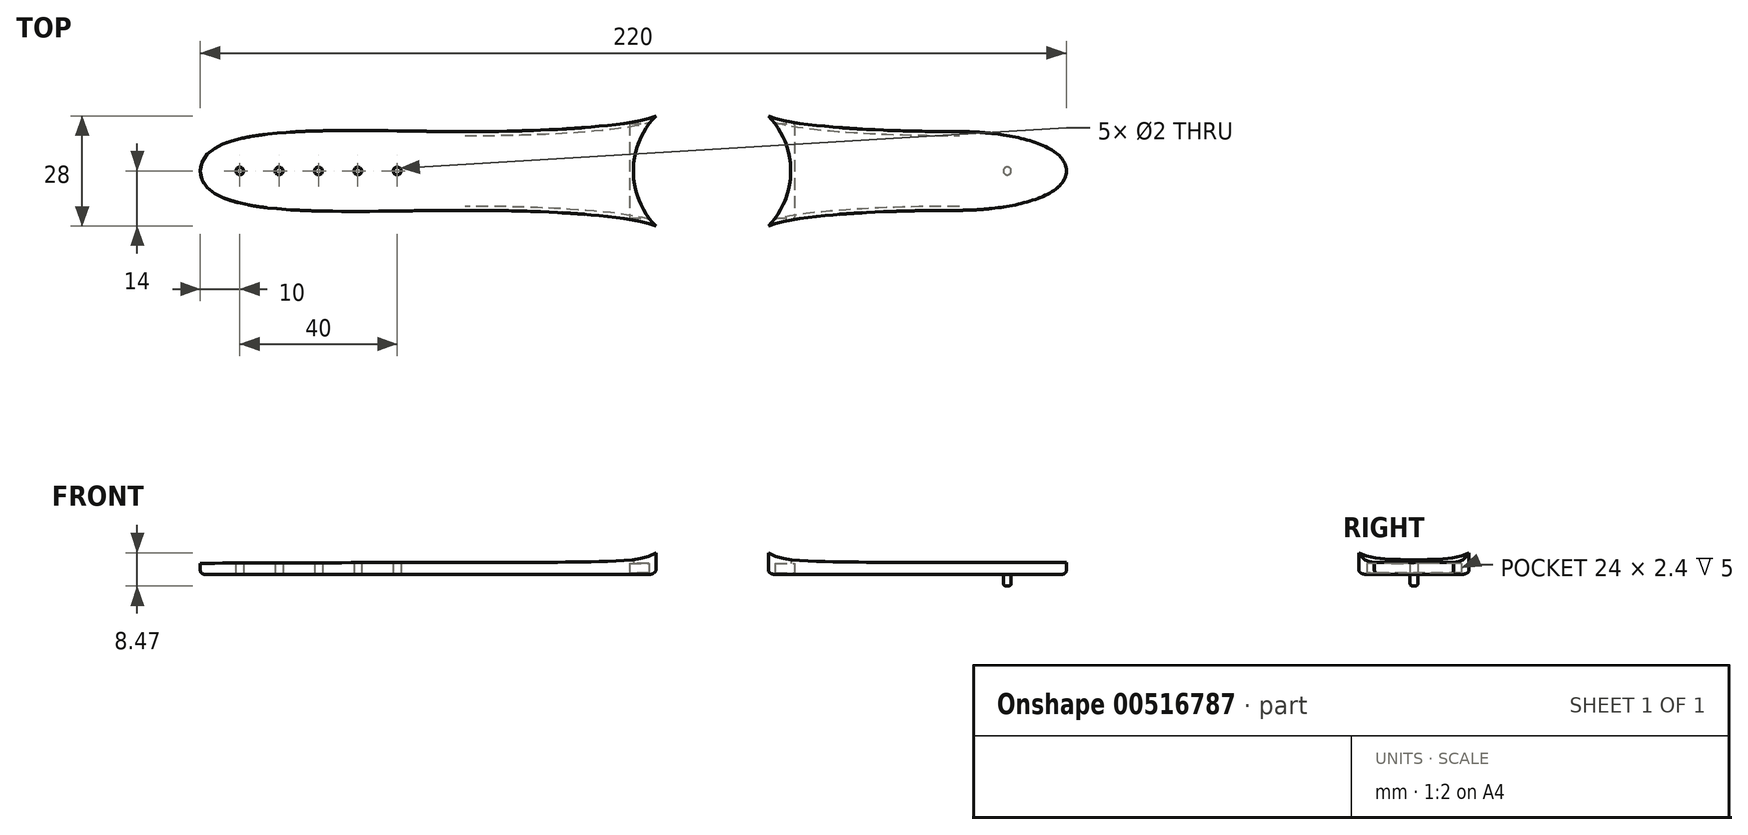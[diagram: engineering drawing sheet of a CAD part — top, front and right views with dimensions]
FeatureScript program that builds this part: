
annotation { "Feature Type Name" : "Feature", "Feature Type Description" : "" }
export const myFeature = defineFeature(function(context is Context, id is Id, definition is map)
    precondition{}
    {
        {
            var Q0;
            Q0=qCreatedBy(makeId("Top.planeOp"),FACE);
            var sketch = newSketch(context, id + "F0", { "sketchPlane" : qUnion([Q0])});
            skArc(sketch, "E0", {"start": v(-14.28, 14) * mm, "mid": v(-20, 0) * mm, "end": v(-14.28, -14) * mm});
            skFitSpline(sketch, "E1", {"points": [v(-14.28, 14) * mm, v(-62.8, 10) * mm], "startDerivative": vector(-9.22, -5.33) * mm, "endDerivative": vector(-87.74, 0) * mm});
            skLineSegment(sketch, "E2", {"start": v(-62.8, 10) * mm, "end": v(-62.8, 10) * mm});
            skFitSpline(sketch, "E3", {"points": [v(-62.8, 10) * mm, v(-130, 0) * mm], "startDerivative": vector(-91.88, 0) * mm, "endDerivative": vector(0, -38.55) * mm});
            skFitSpline(sketch, "E4.MirrorCS", {"points": [v(-14.28, -14) * mm, v(-62.8, -10) * mm], "startDerivative": vector(-9.22, 5.33) * mm, "endDerivative": vector(-87.74, 0) * mm});
            skLineSegment(sketch, "E5.MirrorCS", {"start": v(-62.8, -10) * mm, "end": v(-62.8, -10) * mm});
            skFitSpline(sketch, "E6.MirrorCS", {"points": [v(-62.8, -10) * mm, v(-130, 0) * mm], "startDerivative": vector(-91.88, 0) * mm, "endDerivative": vector(0, 38.55) * mm});
            skArc(sketch, "E7.MirrorCS", {"start": v(14.28, 14) * mm, "mid": v(20, 0) * mm, "end": v(14.28, -14) * mm});
            skFitSpline(sketch, "E8.MirrorCS", {"points": [v(14.28, 14) * mm, v(62.8, 10) * mm], "startDerivative": vector(9.22, -5.33) * mm, "endDerivative": vector(87.74, 0) * mm});
            skFitSpline(sketch, "E9.MirrorCS", {"points": [v(14.28, -14) * mm, v(62.8, -10) * mm], "startDerivative": vector(9.22, 5.33) * mm, "endDerivative": vector(87.74, 0) * mm});
            skLineSegment(sketch, "E10", {"start": v(62.8, 10) * mm, "end": v(62.8, 10) * mm});
            skLineSegment(sketch, "E11.MirrorCS", {"start": v(62.8, -10) * mm, "end": v(62.8, -10) * mm});
            skFitSpline(sketch, "E12.MirrorCS", {"points": [v(62.8, -10) * mm, v(90, 0) * mm], "startDerivative": vector(33.22, 0) * mm, "endDerivative": vector(0, 21.8) * mm});
            skFitSpline(sketch, "E13.MirrorCS", {"points": [v(62.8, 10) * mm, v(90, 0) * mm], "startDerivative": vector(33.22, 0) * mm, "endDerivative": vector(0, -21.8) * mm});
            skSolve(sketch);
        }
        {
            var Q0;
            Q0=qSketchRegion(id+"F0",true);
            extrude(context, id + "F1", {"entities" : qUnion([Q0]), "depth" : (5.5) * mm});
        }
        {
            var Q0;
            Q0=qCreatedBy(makeId("Front.planeOp"),FACE);
            var sketch = newSketch(context, id + "F2", { "sketchPlane" : qUnion([Q0])});
            skLineSegment(sketch, "E14", {"start": v(-133.54, 2.78) * mm, "end": v(-133.54, 10.44) * mm});
            skLineSegment(sketch, "E15", {"start": v(-14.23, 5.5) * mm, "end": v(-25.17, 14.96) * mm});
            skLineSegment(sketch, "E16", {"start": v(-25.17, 14.96) * mm, "end": v(-133.54, 10.44) * mm});
            skLineSegment(sketch, "E17", {"start": v(14.23, 5.5) * mm, "end": v(22.62, 12.49) * mm});
            skLineSegment(sketch, "E18", {"start": v(22.62, 12.49) * mm, "end": v(93.9, 5.99) * mm});
            skPoint(sketch, "E19", {"position": v(-133.54, 2.78) * mm});
            skFitSpline(sketch, "E20.MirrorCS", {"points": [v(14.23, 5.5) * mm, v(80, 3) * mm], "startDerivative": vector(15.03, -7.53) * mm, "endDerivative": vector(188.68, 0) * mm});
            skFitSpline(sketch, "E21.MirrorCS", {"points": [v(-14.23, 5.5) * mm, v(-80, 3) * mm], "startDerivative": vector(-15.03, -7.53) * mm, "endDerivative": vector(-188.68, 0) * mm});
            skLineSegment(sketch, "E22.MirrorCS", {"start": v(-80, 3) * mm, "end": v(-133.54, 2.78) * mm});
            skLineSegment(sketch, "E23", {"start": v(80, 3) * mm, "end": v(80, 3) * mm});
            skLineSegment(sketch, "E24", {"start": v(80, 3) * mm, "end": v(92.32, 3) * mm});
            skLineSegment(sketch, "E25", {"start": v(92.32, 3) * mm, "end": v(93.9, 5.99) * mm});
            skSolve(sketch);
        }
        {
            var Q0;
            Q0=qSketchRegion(id+"F2",true);
            extrude(context, id + "F3", {"entities" : qUnion([Q0]), "operationType" : NewBodyOperationType.REMOVE, "endBound" : BoundingType.SYMMETRIC, "oppositeDirection" : true, "depth" : 40 * mm});
        }
        {
            var Q0;
            Q0=makeQuery(id+"F3.boolean.opBoolean","INTERSECT",EDGE,{"derivedFrom":[makeQuery(id+"F1.opExtrude","SWEPT_FACE",FACE,{"disambiguationData":[OSD([sQuery(id+"F0.wireOp",EDGE,"E1")])]}),makeQuery(id+"F3.opExtrude","SWEPT_FACE",FACE,{"disambiguationData":[OSD([sQuery(id+"F2.wireOp",EDGE,"ddad4ba2-1875-45fb-a996-aad7ab552623")])]})]});
            var Q1;
            Q1=makeQuery(id+"F3.boolean.opBoolean","INTERSECT",EDGE,{"derivedFrom":[makeQuery(id+"F1.opExtrude","SWEPT_FACE",FACE,{"disambiguationData":[OSD([sQuery(id+"F0.wireOp",EDGE,"E3")])]}),makeQuery(id+"F3.opExtrude","SWEPT_FACE",FACE,{"disambiguationData":[OSD([sQuery(id+"F2.wireOp",EDGE,"ddad4ba2-1875-45fb-a996-aad7ab552623")])]})]});
            var Q2;
            Q2=makeQuery(id+"F1.opExtrude","CAP_EDGE",EDGE,{"disambiguationData":[OSD([sQuery(id+"F0.wireOp",EDGE,"E1")])],"isStart":true});
            var Q3;
            Q3=makeQuery(id+"F1.opExtrude","CAP_EDGE",EDGE,{"disambiguationData":[OSD([sQuery(id+"F0.wireOp",EDGE,"E8.MirrorCS")])],"isStart":true});
            var Q4;
            Q4=makeQuery(id+"F1.opExtrude","CAP_EDGE",EDGE,{"disambiguationData":[OSD([sQuery(id+"F0.wireOp",EDGE,"E9.MirrorCS")])],"isStart":true});
            var Q5;
            Q5=makeQuery(id+"F3.boolean.opBoolean","INTERSECT",EDGE,{"derivedFrom":[makeQuery(id+"F1.opExtrude","SWEPT_FACE",FACE,{"disambiguationData":[OSD([sQuery(id+"F0.wireOp",EDGE,"E8.MirrorCS")])]}),makeQuery(id+"F3.opExtrude","SWEPT_FACE",FACE,{"disambiguationData":[OSD([sQuery(id+"F2.wireOp",EDGE,"e5625134-0e9f-45f6-a949-9df659dbd201.MirrorCS")])]})]});
            fillet(context, id + "F4", {"entities" : qUnion([Q0, Q1, Q2, Q3, Q4, Q5]), "radius" : 1 * mm, "tangentPropagation" : true, "allowEdgeOverflow" : false});
        }
        {
            var Q0;
            Q0=qCreatedBy(makeId("Right.planeOp"),FACE);
            var sketch = newSketch(context, id + "F5", { "sketchPlane" : qUnion([Q0])});
            skLineSegment(sketch, "E26.bottom", {"start": v(12, 2.8) * mm, "end": v(-12, 2.8) * mm});
            skLineSegment(sketch, "E26.top", {"start": v(12, 0.4) * mm, "end": v(-12, 0.4) * mm});
            skLineSegment(sketch, "E26.left", {"start": v(12, 2.8) * mm, "end": v(12, 0.4) * mm});
            skLineSegment(sketch, "E26.right", {"start": v(-12, 2.8) * mm, "end": v(-12, 0.4) * mm});
            skSolve(sketch);
        }
        {
            var Q0;
            Q0=qSketchRegion(id+"F5",true);
            extrude(context, id + "F6", {"entities" : qUnion([Q0]), "operationType" : NewBodyOperationType.REMOVE, "endBound" : BoundingType.SYMMETRIC, "oppositeDirection" : true, "depth" : 42 * mm});
        }
        {
            var Q0;
            Q0=makeQuery(id+"F1.opExtrude","CAP_FACE",FACE,{"disambiguationData":[OSD([sQuery(id+"F0.wireOp",EDGE,"E7.MirrorCS"),sQuery(id+"F0.wireOp",EDGE,"E8.MirrorCS"),sQuery(id+"F0.wireOp",EDGE,"E9.MirrorCS"),sQuery(id+"F0.wireOp",EDGE,"E12.MirrorCS"),sQuery(id+"F0.wireOp",EDGE,"E13.MirrorCS")])],"isStart":true});
            var sketch = newSketch(context, id + "F7", { "sketchPlane" : qUnion([Q0])});
            skCircle(sketch, "E27", {"center": v(75, 0) * mm, "radius": 1 * mm});
            skSolve(sketch);
        }
        {
            var Q0;
            Q0=makeQuery(id+"F7.imprint","IMPRINT",FACE,{"disambiguationData":[TD([[makeQuery(id+"F7.imprint","IMPRINT",EDGE,{"derivedFrom":sQuery(id+"F7.wireOp",EDGE,"E27")}),1.0]])]});
            extrude(context, id + "F8", {"entities" : qUnion([Q0]), "operationType" : NewBodyOperationType.ADD, "depth" : 3 * mm});
        }
        {
            var Q0;
            Q0=makeQuery(id+"F8.opExtrude","CAP_FACE",FACE,{"disambiguationData":[OSD([sQuery(id+"F7.wireOp",EDGE,"E27")])],"isStart":false});
            fillet(context, id + "F9", {"entities" : qUnion([Q0]), "radius" : 0.7 * mm, "tangentPropagation" : true, "allowEdgeOverflow" : false});
        }
        {
            var Q0;
            Q0=makeQuery(id+"F1.opExtrude","CAP_FACE",FACE,{"disambiguationData":[OSD([sQuery(id+"F0.wireOp",EDGE,"E0"),sQuery(id+"F0.wireOp",EDGE,"E1"),sQuery(id+"F0.wireOp",EDGE,"E3"),sQuery(id+"F0.wireOp",EDGE,"E4.MirrorCS"),sQuery(id+"F0.wireOp",EDGE,"E6.MirrorCS")])],"isStart":true});
            var sketch = newSketch(context, id + "F10", { "sketchPlane" : qUnion([Q0])});
            skPoint(sketch, "E28", {"position": v(-80, 0) * mm});
            skPoint(sketch, "E29", {"position": v(-90, 0) * mm});
            skPoint(sketch, "E30", {"position": v(-100, 0) * mm});
            skPoint(sketch, "E31", {"position": v(-110, 0) * mm});
            skPoint(sketch, "E32", {"position": v(-120, 0) * mm});
            skSolve(sketch);
        }
        {
            var Q0;
            Q0=sQuery(id+"F10.wireOp",VERTEX,"E32");
            var Q1;
            Q1=sQuery(id+"F10.wireOp",VERTEX,"E31");
            var Q2;
            Q2=sQuery(id+"F10.wireOp",VERTEX,"E30");
            var Q3;
            Q3=sQuery(id+"F10.wireOp",VERTEX,"E29");
            var Q4;
            Q4=sQuery(id+"F10.wireOp",VERTEX,"E28");
            var Q5;
            Q5=makeQuery(id+"F1.opExtrude","SWEPT_BODY",BODY,{"disambiguationData":[OSD([sQuery(id+"F0.wireOp",EDGE,"E0"),sQuery(id+"F0.wireOp",EDGE,"E1"),sQuery(id+"F0.wireOp",EDGE,"E3"),sQuery(id+"F0.wireOp",EDGE,"E4.MirrorCS"),sQuery(id+"F0.wireOp",EDGE,"E6.MirrorCS")])]});
            hole(context, id + "F11", {"style" : HoleStyle.SIMPLE, "endStyle" : HoleEndStyle.THROUGH, "holeDiameter" : 2 * mm, "isTappedThrough" : true, "tappedDepth" : 12 * mm, "tapClearance" : 3, "locations" : qUnion([Q0, Q1, Q2, Q3, Q4]), "scope" : qUnion([Q5])});
        }
    });
